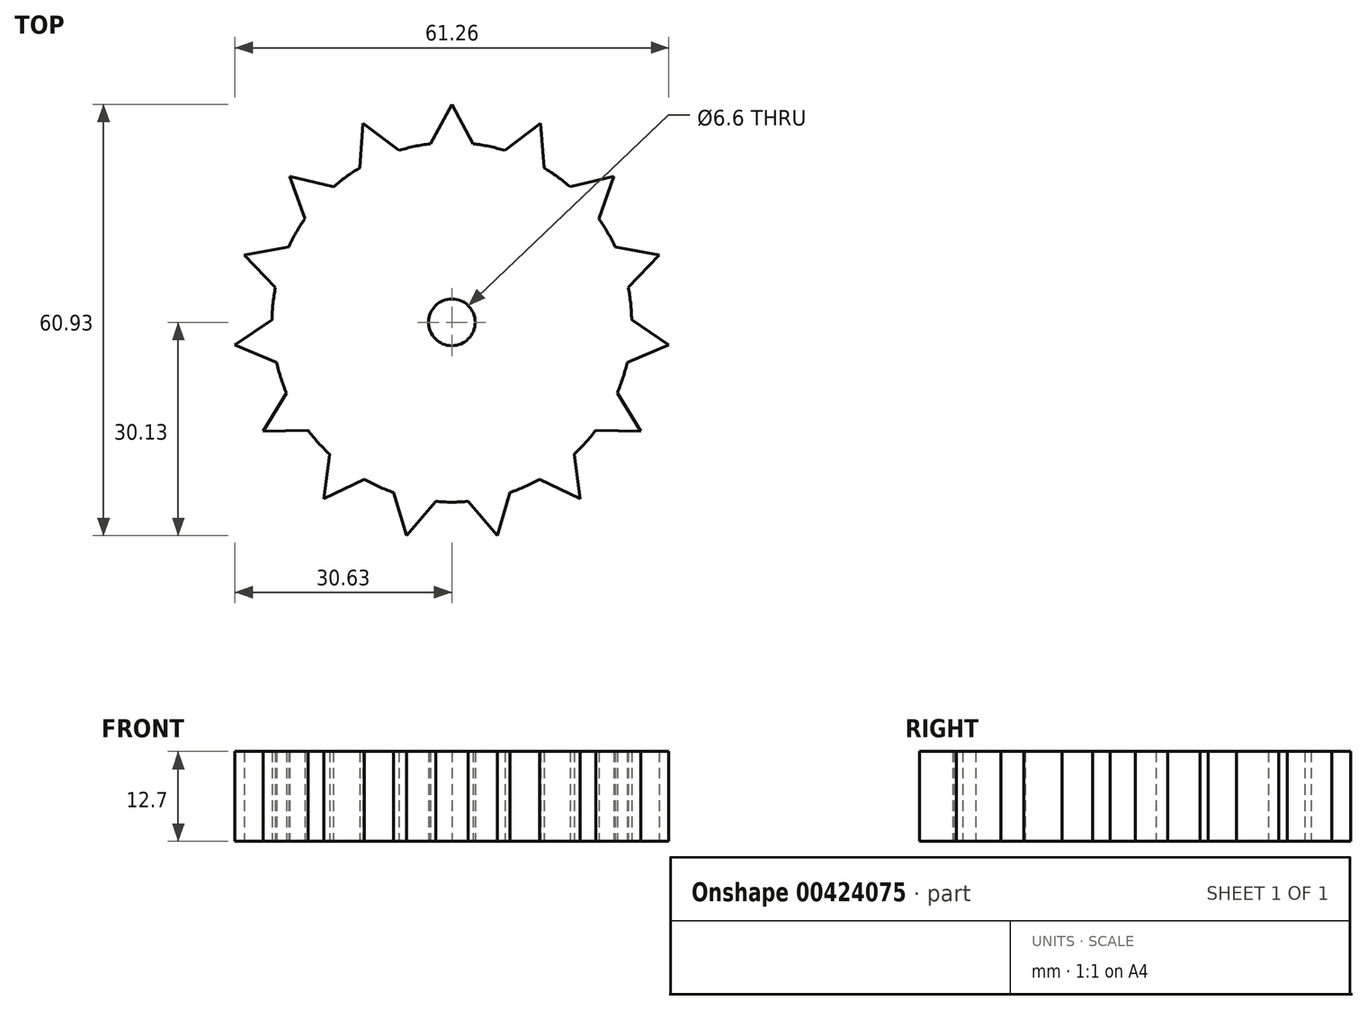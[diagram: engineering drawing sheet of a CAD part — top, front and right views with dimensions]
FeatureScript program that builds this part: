
annotation { "Feature Type Name" : "Feature", "Feature Type Description" : "" }
export const myFeature = defineFeature(function(context is Context, id is Id, definition is map)
    precondition{}
    {
        {
            var Q0;
            Q0=qCreatedBy(makeId("Top.planeOp"),FACE);
            var sketch = newSketch(context, id + "F0", { "sketchPlane" : qUnion([Q0])});
            skCircle(sketch, "E0", {"center": v(0, 0) * mm, "radius": 25.4 * mm});
            skCircle(sketch, "E1", {"center": v(0, 0) * mm, "radius": 3.3 * mm});
            skLineSegment(sketch, "E2", {"start": v(-3.03, 25.22) * mm, "end": v(0, 30.8) * mm});
            skLineSegment(sketch, "E3", {"start": v(0, 30.8) * mm, "end": v(3.03, 25.22) * mm});
            skLineSegment(sketch, "E4.1.0", {"start": v(-13.02, 21.8) * mm, "end": v(-12.53, 28.14) * mm});
            skLineSegment(sketch, "E4.1.1", {"start": v(-12.53, 28.14) * mm, "end": v(-7.5, 24.27) * mm});
            skLineSegment(sketch, "E4.2.0", {"start": v(-20.77, 14.62) * mm, "end": v(-22.89, 20.6) * mm});
            skLineSegment(sketch, "E4.2.1", {"start": v(-22.89, 20.6) * mm, "end": v(-16.72, 19.12) * mm});
            skLineSegment(sketch, "E4.3.0", {"start": v(-24.92, 4.91) * mm, "end": v(-29.3, 9.52) * mm});
            skLineSegment(sketch, "E4.3.1", {"start": v(-29.3, 9.52) * mm, "end": v(-23.05, 10.67) * mm});
            skLineSegment(sketch, "E4.4.0", {"start": v(-24.76, -5.65) * mm, "end": v(-30.63, -3.22) * mm});
            skLineSegment(sketch, "E4.4.1", {"start": v(-30.63, -3.22) * mm, "end": v(-25.4, 0.38) * mm});
            skLineSegment(sketch, "E4.5.0", {"start": v(-20.33, -15.23) * mm, "end": v(-26.67, -15.4) * mm});
            skLineSegment(sketch, "E4.5.1", {"start": v(-26.67, -15.4) * mm, "end": v(-23.35, -9.99) * mm});
            skLineSegment(sketch, "E4.6.0", {"start": v(-12.37, -22.18) * mm, "end": v(-18.1, -24.92) * mm});
            skLineSegment(sketch, "E4.6.1", {"start": v(-18.1, -24.92) * mm, "end": v(-17.27, -18.62) * mm});
            skLineSegment(sketch, "E4.7.0", {"start": v(-2.28, -25.3) * mm, "end": v(-6.4, -30.13) * mm});
            skLineSegment(sketch, "E4.7.1", {"start": v(-6.4, -30.13) * mm, "end": v(-8.2, -24.04) * mm});
            skLineSegment(sketch, "E4.8.0", {"start": v(8.2, -24.04) * mm, "end": v(6.4, -30.13) * mm});
            skLineSegment(sketch, "E4.8.1", {"start": v(6.4, -30.13) * mm, "end": v(2.28, -25.3) * mm});
            skLineSegment(sketch, "E4.9.0", {"start": v(17.27, -18.62) * mm, "end": v(18.1, -24.92) * mm});
            skLineSegment(sketch, "E4.9.1", {"start": v(18.1, -24.92) * mm, "end": v(12.37, -22.18) * mm});
            skLineSegment(sketch, "E4.10.0", {"start": v(23.35, -9.99) * mm, "end": v(26.67, -15.4) * mm});
            skLineSegment(sketch, "E4.10.1", {"start": v(26.67, -15.4) * mm, "end": v(20.33, -15.23) * mm});
            skLineSegment(sketch, "E4.11.0", {"start": v(25.4, 0.38) * mm, "end": v(30.63, -3.22) * mm});
            skLineSegment(sketch, "E4.11.1", {"start": v(30.63, -3.22) * mm, "end": v(24.76, -5.65) * mm});
            skLineSegment(sketch, "E4.12.0", {"start": v(23.05, 10.67) * mm, "end": v(29.3, 9.52) * mm});
            skLineSegment(sketch, "E4.12.1", {"start": v(29.3, 9.52) * mm, "end": v(24.92, 4.91) * mm});
            skLineSegment(sketch, "E4.13.0", {"start": v(16.72, 19.12) * mm, "end": v(22.89, 20.6) * mm});
            skLineSegment(sketch, "E4.13.1", {"start": v(22.89, 20.6) * mm, "end": v(20.77, 14.62) * mm});
            skLineSegment(sketch, "E4.14.0", {"start": v(7.5, 24.27) * mm, "end": v(12.53, 28.14) * mm});
            skLineSegment(sketch, "E4.14.1", {"start": v(12.53, 28.14) * mm, "end": v(13.02, 21.8) * mm});
            skSolve(sketch);
        }
        {
            var Q0;
            Q0 = qSketchRegion(id + "F0", true);
            extrude(context, id + "F1", {"entities" : qUnion([Q0]), "depth" : 12.7 * mm});
        }
    });
